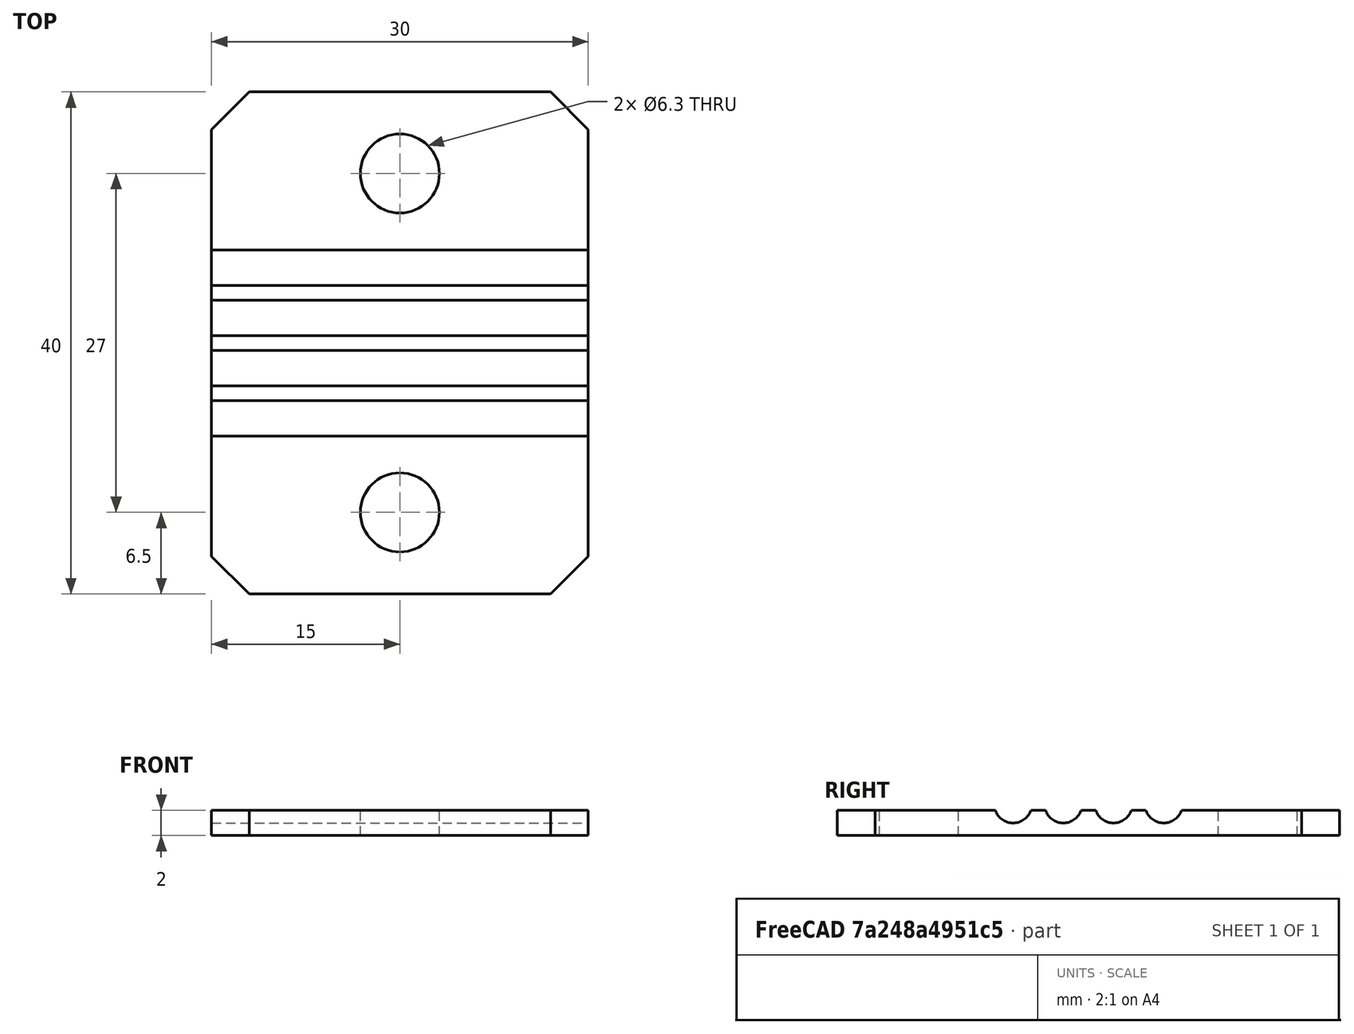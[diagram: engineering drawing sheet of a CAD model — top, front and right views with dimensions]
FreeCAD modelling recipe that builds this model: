
FCSTD DOCUMENT  (FreeCAD 0.15R4671 (Git))
Label: two_tendon_strap
License: All rights reserved
LicenseURL: http://en.wikipedia.org/wiki/All_rights_reserved
objects: Part::Cylinder×6, Part::Box×1, Part::MultiFuse×1, Part::Cut×1, Part::Chamfer×1
note: 10 computed .brp shape members not serialized (recipe doc carries the construction recipe); baked Part::Feature solids carry a one-line shape summary decoded from their .brp

FEATURE [Part::Box] Box  label="Cube"
  Height = 2
  Length = 30
  Width = 40
FEATURE [Part::Cylinder] Cylinder
  Angle = 360
  Height = 40
  Placement = pos=(-2,18,2.5) rot=(0,1,0;1.5708rad)
  Radius = 1.5
FEATURE [Part::Cylinder] Cylinder001
  Angle = 360
  Height = 40
  Placement = pos=(-2,22,2.5) rot=(0,1,0;1.5708rad)
  Radius = 1.5
FEATURE [Part::Cylinder] Cylinder002
  Angle = 360
  Height = 40
  Placement = pos=(-2,14,2.5) rot=(0,1,0;1.5708rad)
  Radius = 1.5
FEATURE [Part::Cylinder] Cylinder003
  Angle = 360
  Height = 40
  Placement = pos=(-2,26,2.5) rot=(0,1,0;1.5708rad)
  Radius = 1.5
FEATURE [Part::Cylinder] Cylinder004
  Angle = 360
  Height = 10
  Placement = pos=(15,6.5,-2) rot=(0,0,1;0rad)
  Radius = 3.15
FEATURE [Part::Cylinder] Cylinder005
  Angle = 360
  Height = 10
  Placement = pos=(15,33.5,-2) rot=(0,0,1;0rad)
  Radius = 3.15
FEATURE [Part::MultiFuse] Fusion
  Shapes = -> [Cylinder,Cylinder003,Cylinder001,Cylinder005,Cylinder004,Cylinder002]
FEATURE [Part::Cut] Cut
  Base = -> Box
  Tool = -> Fusion
FEATURE [Part::Chamfer] Chamfer
  Base = -> Cut
  Edges = 4 edges r=3: [Edge14,Edge16,Edge47,Edge52]
